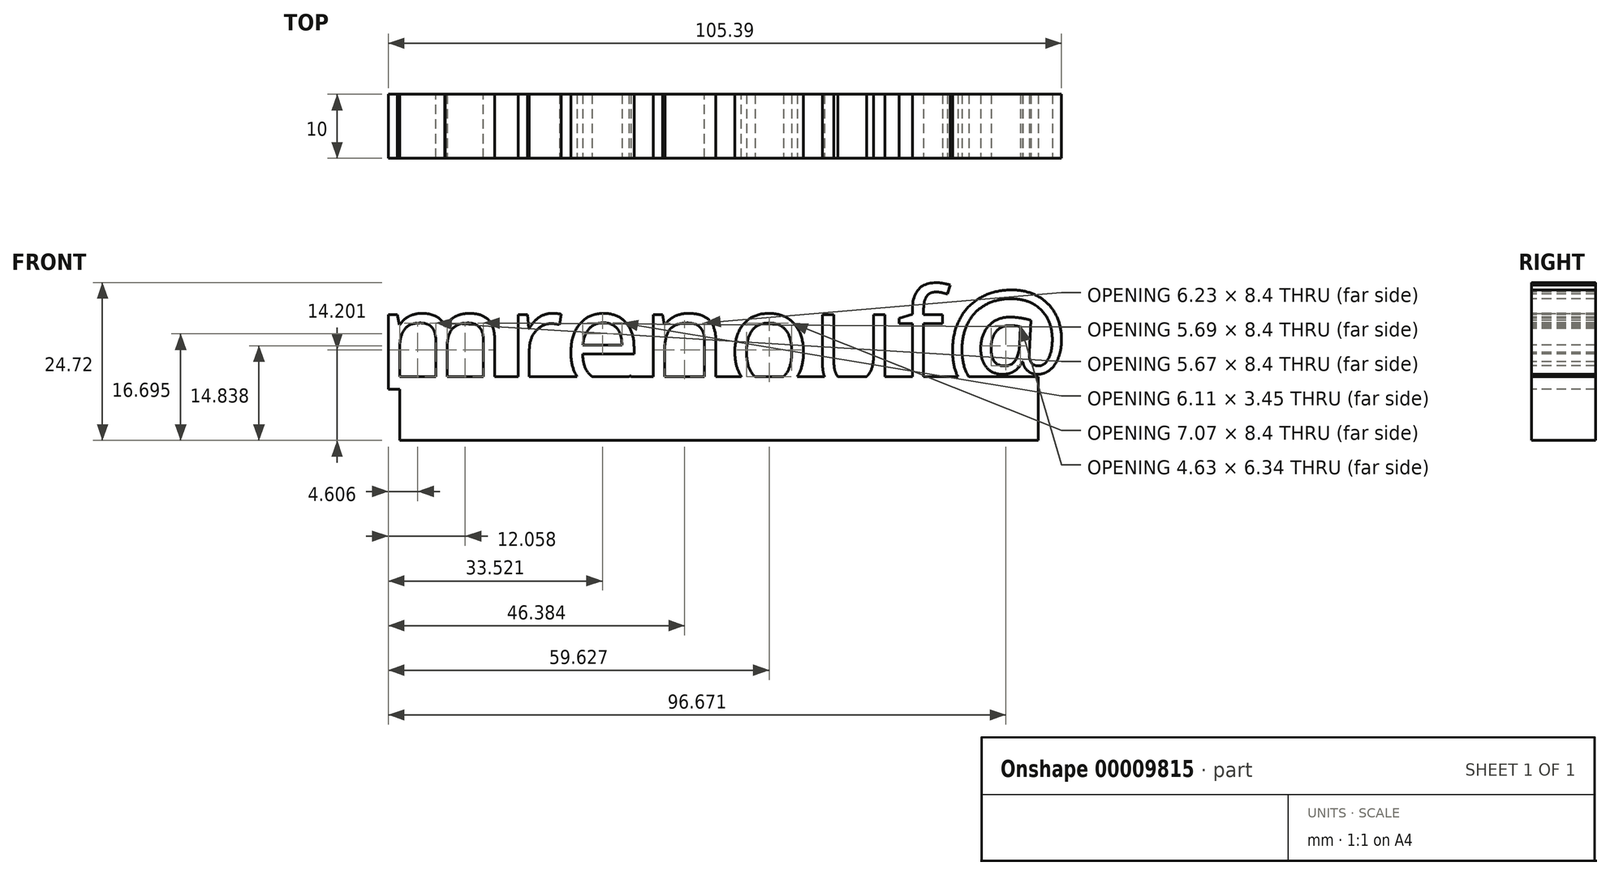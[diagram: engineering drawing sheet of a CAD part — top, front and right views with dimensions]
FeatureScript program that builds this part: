
annotation { "Feature Type Name" : "Feature", "Feature Type Description" : "" }
export const myFeature = defineFeature(function(context is Context, id is Id, definition is map)
    precondition{}
    {
        {
            var Q0;
            Q0=qCreatedBy(makeId("Top.planeOp"),FACE);
            var sketch = newSketch(context, id + "F0", { "sketchPlane" : qUnion([Q0])});
            skLineSegment(sketch, "E0.rect.bottom", {"start": v(50, -21.98) * mm, "end": v(-50, -21.98) * mm});
            skLineSegment(sketch, "E0.rect.top", {"start": v(50, -31.98) * mm, "end": v(-50, -31.98) * mm});
            skLineSegment(sketch, "E0.rect.left", {"start": v(50, -21.98) * mm, "end": v(50, -31.98) * mm});
            skLineSegment(sketch, "E0.rect.right", {"start": v(-50, -21.98) * mm, "end": v(-50, -31.98) * mm});
            skPoint(sketch, "E0.rect.middle", {"position": v(0, -1.13) * mm});
            skSolve(sketch);
        }
        {
            var Q0;
            Q0=makeQuery(id+"F0.imprint","IMPRINT",FACE,{"disambiguationData":[TD([[makeQuery(id+"F0.imprint","IMPRINT",EDGE,{"derivedFrom":sQuery(id+"F0.wireOp",EDGE,"E0.rect.bottom")}),1.0]])]});
            extrude(context, id + "F1", {"entities" : qUnion([Q0]), "depth" : 10 * mm});
        }
        {
            var Q0;
            Q0=makeQuery(id+"F1.opExtrude","SWEPT_FACE",FACE,{"disambiguationData":[OSD([sQuery(id+"F0.wireOp",EDGE,"E0.rect.top")])]});
            var sketch = newSketch(context, id + "F2", { "sketchPlane" : qUnion([Q0])});
            skText(sketch, "E1", { "text": "mrenouf@", "fontName": "OpenSans-Regular.ttf"});
            const initialGuessF2  = {"E1": [-0.05365, 0.008, 1, 0, 0.01573]};
            skSetInitialGuess(sketch, initialGuessF2);
            skSolve(sketch);
        }
        {
            var Q0;
            Q0 = qSketchRegion(id + "F2", true);
            extrude(context, id + "F3", {"entities" : qUnion([Q0]), "operationType" : NewBodyOperationType.ADD, "oppositeDirection" : true, "depth" : 10 * mm});
        }
    });
